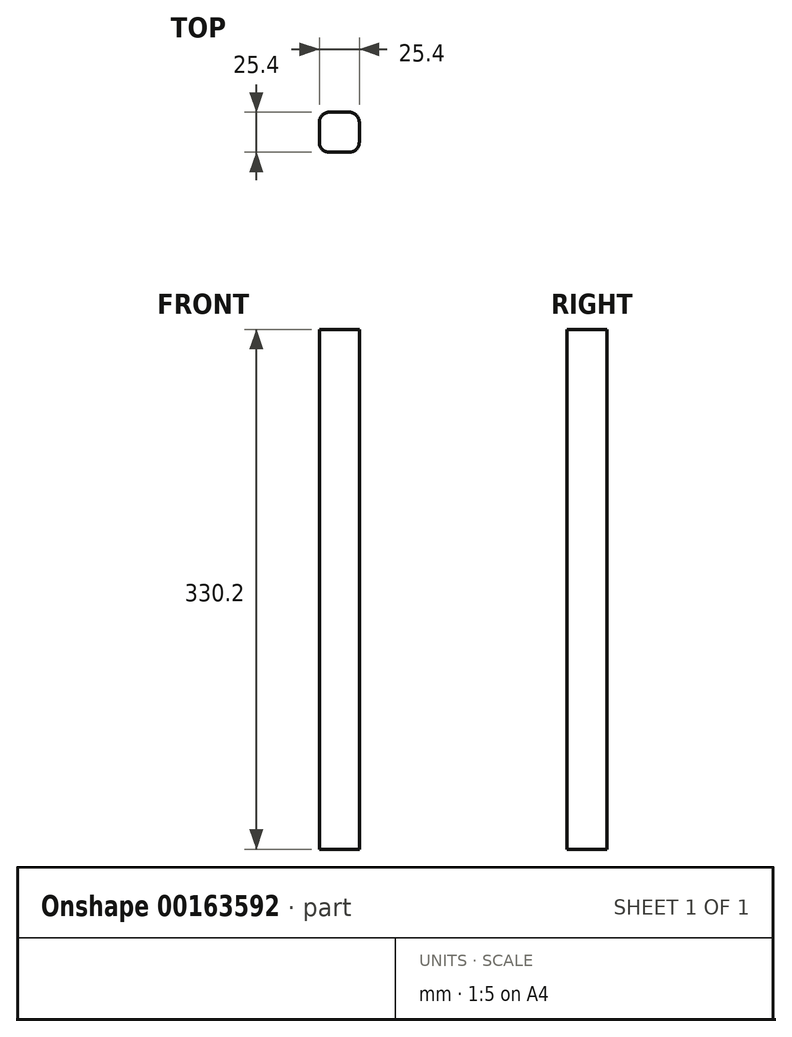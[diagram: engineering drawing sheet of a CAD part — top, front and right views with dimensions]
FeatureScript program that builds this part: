
annotation { "Feature Type Name" : "Feature", "Feature Type Description" : "" }
export const myFeature = defineFeature(function(context is Context, id is Id, definition is map)
    precondition{}
    {
        {
            var Q0;
            Q0=qCreatedBy(makeId("Top.planeOp"),FACE);
            var sketch = newSketch(context, id + "F0", { "sketchPlane" : qUnion([Q0])});
            skLineSegment(sketch, "E0.bottom", {"start": v(6.35, 12.7) * mm, "end": v(-6.35, 12.7) * mm});
            skLineSegment(sketch, "E0.top", {"start": v(6.35, -12.7) * mm, "end": v(-6.35, -12.7) * mm});
            skLineSegment(sketch, "E0.left", {"start": v(12.7, 6.35) * mm, "end": v(12.7, -6.35) * mm});
            skLineSegment(sketch, "E0.right", {"start": v(-12.7, 6.35) * mm, "end": v(-12.7, -6.35) * mm});
            skPoint(sketch, "E0.middle", {"position": v(0, 0) * mm});
            skPoint(sketch, "E1.visualSharp", {"position": v(-12.7, 12.7) * mm});
            skArc(sketch, "E1.filletArc", {"start": v(-6.35, 12.7) * mm, "mid": v(-10.84, 10.84) * mm, "end": v(-12.7, 6.35) * mm});
            skPoint(sketch, "E2.visualSharp", {"position": v(-12.7, -12.7) * mm});
            skArc(sketch, "E2.filletArc", {"start": v(-12.7, -6.35) * mm, "mid": v(-10.84, -10.84) * mm, "end": v(-6.35, -12.7) * mm});
            skPoint(sketch, "E3.visualSharp", {"position": v(12.7, -12.7) * mm});
            skArc(sketch, "E3.filletArc", {"start": v(6.35, -12.7) * mm, "mid": v(10.84, -10.84) * mm, "end": v(12.7, -6.35) * mm});
            skPoint(sketch, "E4.visualSharp", {"position": v(12.7, 12.7) * mm});
            skArc(sketch, "E4.filletArc", {"start": v(12.7, 6.35) * mm, "mid": v(10.84, 10.84) * mm, "end": v(6.35, 12.7) * mm});
            skSolve(sketch);
        }
        {
            var Q0;
            Q0=qSketchRegion(id+"F0",true);
            extrude(context, id + "F1", {"entities" : qUnion([Q0]), "depth" : 330.2 * mm, "offsetDistance" : 25.4 * mm});
        }
    });
